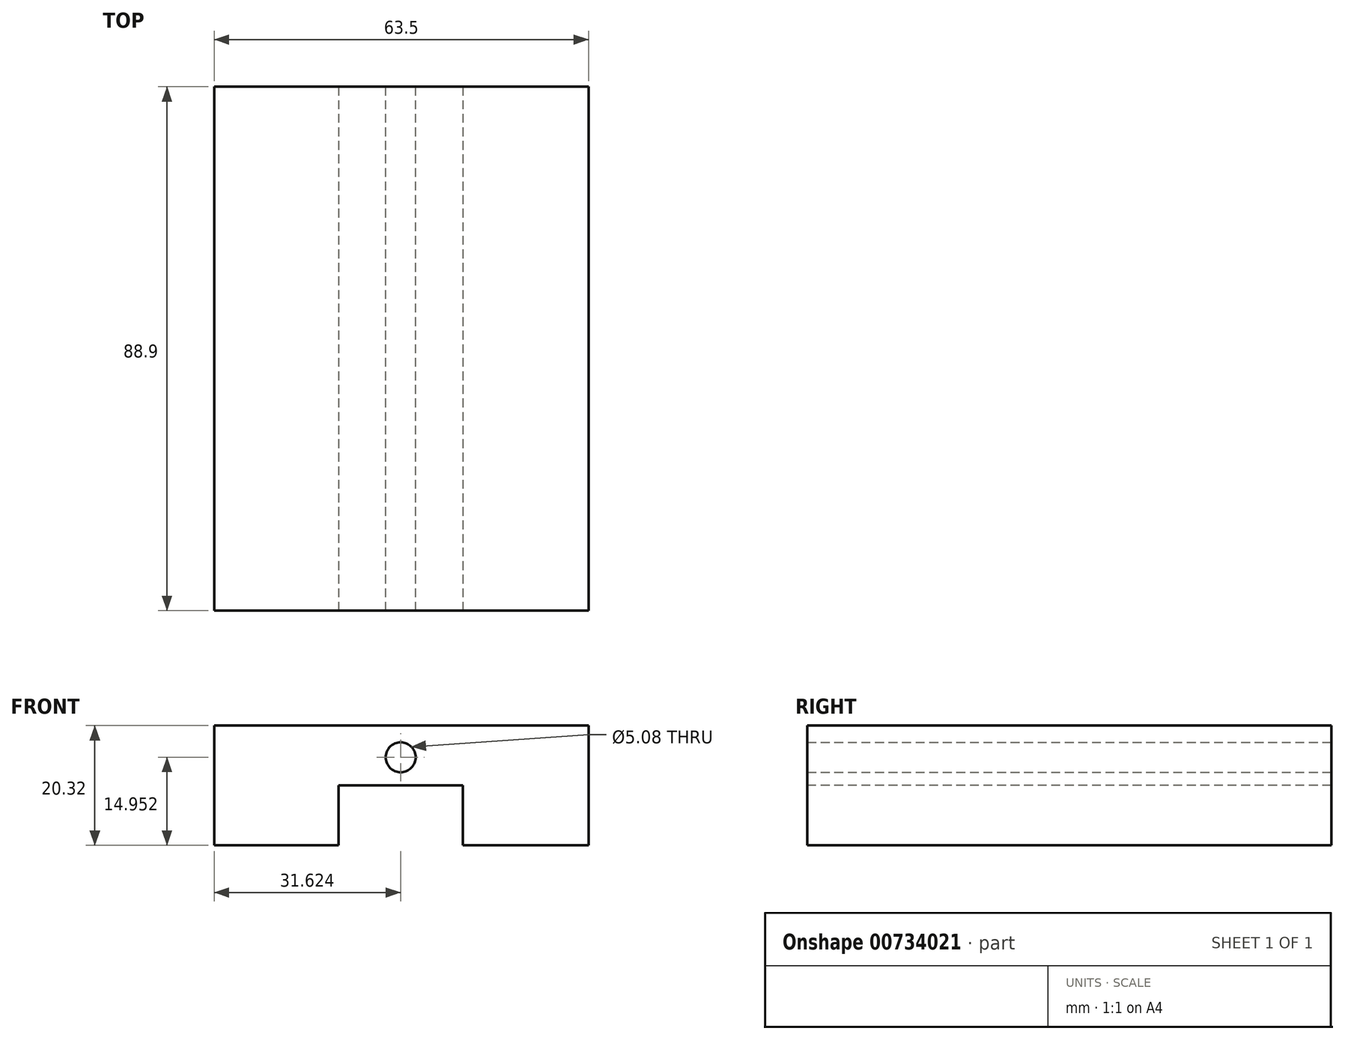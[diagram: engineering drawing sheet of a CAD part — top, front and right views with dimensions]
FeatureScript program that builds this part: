
annotation { "Feature Type Name" : "Feature", "Feature Type Description" : "" }
export const myFeature = defineFeature(function(context is Context, id is Id, definition is map)
    precondition{}
    {
        {
            var Q0;
            Q0=qCreatedBy(makeId("Top.planeOp"),FACE);
            var sketch = newSketch(context, id + "F0", { "sketchPlane" : qUnion([Q0])});
            skLineSegment(sketch, "E0.bottom", {"start": v(-34.24, 48.06) * mm, "end": v(29.26, 48.06) * mm});
            skLineSegment(sketch, "E0.top", {"start": v(-34.24, -40.84) * mm, "end": v(29.26, -40.84) * mm});
            skLineSegment(sketch, "E0.left", {"start": v(-34.24, 48.06) * mm, "end": v(-34.24, -40.84) * mm});
            skLineSegment(sketch, "E0.right", {"start": v(29.26, 48.06) * mm, "end": v(29.26, -40.84) * mm});
            skLineSegment(sketch, "E1", {"start": v(-13.16, 48.06) * mm, "end": v(-13.16, -40.84) * mm});
            skLineSegment(sketch, "E2", {"start": v(7.93, 48.06) * mm, "end": v(7.93, -40.84) * mm});
            skSolve(sketch);
        }
        {
            var Q0;
            Q0=makeQuery(id+"F0.imprint","IMPRINT",FACE,{"disambiguationData":[TD([[makeQuery(id+"F0.imprint","IMPRINT",EDGE,{"derivedFrom":sQuery(id+"F0.wireOp",EDGE,"E0.bottom")}),-1.0]])]});
            extrude(context, id + "F1", {"entities" : qUnion([Q0]), "depth" : 20.32 * mm, "offsetDistance" : 25.4 * mm});
        }
        {
            var Q0;
            {var subQ0=sQuery(id+"F0.wireOp",EDGE,"E1");Q0=makeQuery(id+"F0.imprint","IMPRINT",FACE,{"disambiguationData":[TD([[makeQuery(id+"F0.imprint","IMPRINT",EDGE,{"derivedFrom":subQ0}),1.0]])]});}
            extrude(context, id + "F2", {"entities" : qUnion([Q0]), "operationType" : NewBodyOperationType.REMOVE, "depth" : 10.16 * mm, "offsetDistance" : 25.4 * mm});
        }
        {
            var Q0;
            Q0=makeQuery(id+"F1.opExtrude","SWEPT_FACE",FACE,{"disambiguationData":[OSD([sQuery(id+"F0.wireOp",EDGE,"E0.bottom")])]});
            var sketch = newSketch(context, id + "F3", { "sketchPlane" : qUnion([Q0])});
            skCircle(sketch, "E3", {"center": v(2.62, 14.95) * mm, "radius": 2.54 * mm});
            skPoint(sketch, "E3.centerSnap0", {"position": v(2.62, 10.16) * mm});
            skSolve(sketch);
        }
        {
            var Q0;
            Q0=sQuery(id+"F3.wireOp",EDGE,"E3");
            extrude(context, id + "F4", {"bodyType" : ToolBodyType.SURFACE, "surfaceEntities" : qUnion([Q0]), "oppositeDirection" : true, "depth" : 88.9 * mm, "offsetDistance" : 25.4 * mm});
        }
        {
            var Q0;
            Q0 = qSketchRegion(id + "F3", true);
            extrude(context, id + "F5", {"entities" : qUnion([Q0]), "operationType" : NewBodyOperationType.REMOVE, "oppositeDirection" : true, "depth" : 88.9 * mm, "offsetDistance" : 25.4 * mm});
        }
    });
